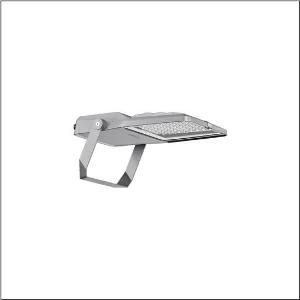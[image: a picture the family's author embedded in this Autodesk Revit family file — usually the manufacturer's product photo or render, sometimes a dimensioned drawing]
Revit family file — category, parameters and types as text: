
# Revit family: floodlight_fl_21_iq_mini___pl43_5xa7771c2a1a_27d2
name_source: partatom
category: Lighting Fixtures
units: mm (PartAtom-declared; Revit-internal decimal feet)

## family parameters
Cut with Voids When Loaded = No
Host = Face
Light Source = No
Part Type = Normal
Room Calculation Point = No
Round Connector Dimension = Use Diameter
Shared = No

## types (1)
- --- (1 x LED, 12520 lm, 87.2 W, 3000K)
    Apparent Load = 87 VA
    CIE Flux Codes = 27 78 99 100 100
    Color Rendering = 70
    Color Temperature = 3000K
    Default Elevation = 1800 mm
    Description = Floodlight FL 21 iQ mini, floodlight, primary light control with lens, of PMMA, primary optical cover: protective disc, of toughened safety glass, transparent, light distribution: PL43, light emission: direct distribution, installation type: surface-mounted, LED, High Power LED, rated luminous flux: 12.520lm, luminous efficacy: 144lm/W, light colour: 730, colour temperature: 3000K, control: Auto-Match, Temp-Guard, Lumen-Switch, Night-Set, Smart-Wire, Light-Fading, Desk-Remote (wireless, voltage-free reading and setting of iQ features in the workshop via application-optimized NFC function/RFID function), optimised constant luminous flux control (CLO 2.0), with terminal, 6-pole, mains connection: 220..240V, AC, 50/60Hz, start of lifetime: 87W, end of service life: 92W, reduction: 40W, luminaire housing, of diecast aluminium, powder-coated, Siteco® metallic grey (DB 702S), corrosivity category C5 mid according to DIN EN ISO 12944, sealing non-destructively replaceable, mounting bracket, of steel, galvanised, powder-coated, Siteco® metallic grey (DB 702S), protection rating (complete): IP66, insulation class (complete): insulation class II (safety insulation), certification: CE, ENEC, VDE, protection symbol: D, impact resistance: IK08, permissible operating ambient temperature: -40..+40°C, permissible operating ambient temperature for outdoor applications: -40..+50°C, standard: DIN EN 12944, LABS conformity tested according to VDMA 24364:2018-05, packaging unit: 1 piece

Light Distribution: PL43
    Height = 70 mm
    Lamp = 1 x LED
    Lamp Light Flux = 12520 lm
    Lamp Power = 87.2 W
    Lamp count = 1
    Length = 485 mm
    Luminous efficacy = 144 lm/W
    Manufacturer = Siteco
    ModVariant = No
    Model = 5XA7771C2A1A
    Number of Poles = 1
    OnlyDefault = Yes
    Power Factor = 1
    Product Name = Floodlight FL 21 iQ mini | PL43
    Product group = floodlight | pylon annexe
    ProductGroupID = 6200
    Protection Class = Protection class II
    Protection Degree = IP 66
    RLX_Detail_Level = 1
    RLX_Emergency_Light_Flux = 0 lm
    RLX_Emergency_Type = 0
    RLX_Emergency_Type_DB = No
    RlxData = <blob elided: 96185 chars, md5=9b6e1d39>
    Socket = socket
    Standby Power = 0 W
    System Light Flux = 12520 lm
    System Power = 87 W
    Type Comments = factory setting: luminous flux: 100 % | dim-lin: 254 | 456 mA
    Type Image = l_1006845.jpg
    URL = http://relux.com
    VarID = @adj_094909
    Voltage = 0 V
    Weight = 0.00 kg
    Width = 337 mm

## geometry (parser evidence)
native form markers: Blend x4, Sweep x10
no freeform markers — native parametric forms only
